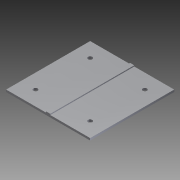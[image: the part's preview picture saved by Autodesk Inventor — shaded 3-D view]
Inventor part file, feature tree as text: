
AUTODESK INVENTOR PART (.ipt)
format: ipt  version: 2011 (Build 150239000, 239)  size: 107,008 bytes
history: native  units: in
note: dims shown in document units (in); Inventor stores cm internally (conversion verified against a paired STEP export)
features: sketch x4, extrude x3
ambient origin geometry x8: Origin, YZ Plane, XZ Plane, XY Plane, X Axis, Y Axis, Z Axis, Center Point
bodies: Solid1 (feature_tree)
feature tree (7):
  sketch  "Sketch1"  dims[d0=20.0in d1=20.0in]
  extrude  "Extrusion1"  Depth=20.0in
  extrude  "Extrusion2"  Depth=3.5in
  extrude  "Extrusion3"  Depth=3.5in
  sketch  "Sketch2"  dims[d2=0.5in d3=0.0in d4=3.5in]
  sketch  "Sketch3"  dims[d5=3.5in d6=3.5in]
  sketch  "Sketch4"  dims[d7=3.5in d8=3.5in d9=3.5in d10=3.5in d11=3.5in d12=1.0in d13=1.0in d14=1.0in d15=1.0in d16=0.5in d17=0.0in d18=10.0in d19=1.0in d20=0.5in d21=1.0in d22=0.25in d23=0.0in]
